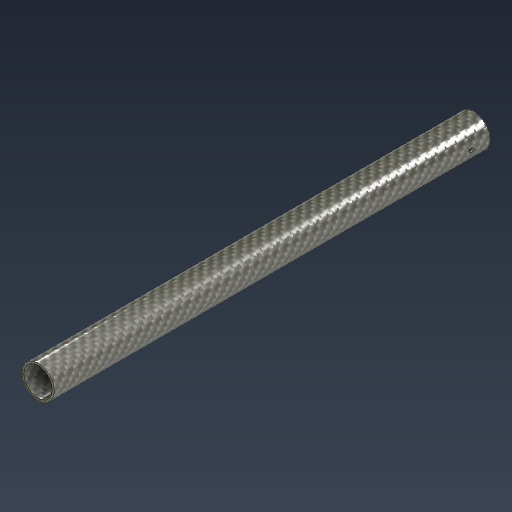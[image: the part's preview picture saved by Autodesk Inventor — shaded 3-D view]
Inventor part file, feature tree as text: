
AUTODESK INVENTOR PART (.ipt)
format: ipt  version: 2025 (Build 290162010, 162A)  size: 161,792 bytes
history: native  units: mm
features: extrude x2, sketch x1
ambient origin geometry x8: Origin, YZ Plane, XZ Plane, XY Plane, X Axis, Y Axis, Z Axis, Center Point
bodies: Solid1 (feature_tree)
feature tree (3):
  extrude  "Extrusion1"  Depth=14.4mm
  extrude  "Extrusion3"  Depth=14.4mm TaperAngle=0.0deg
  sketch  "Sketch3"  dims[d0=25.0mm d1=22.0mm d2=335.7175mm d3=0.0mm d9=3.2mm d10=25.0mm d11=0.0mm d12=14.4mm]
